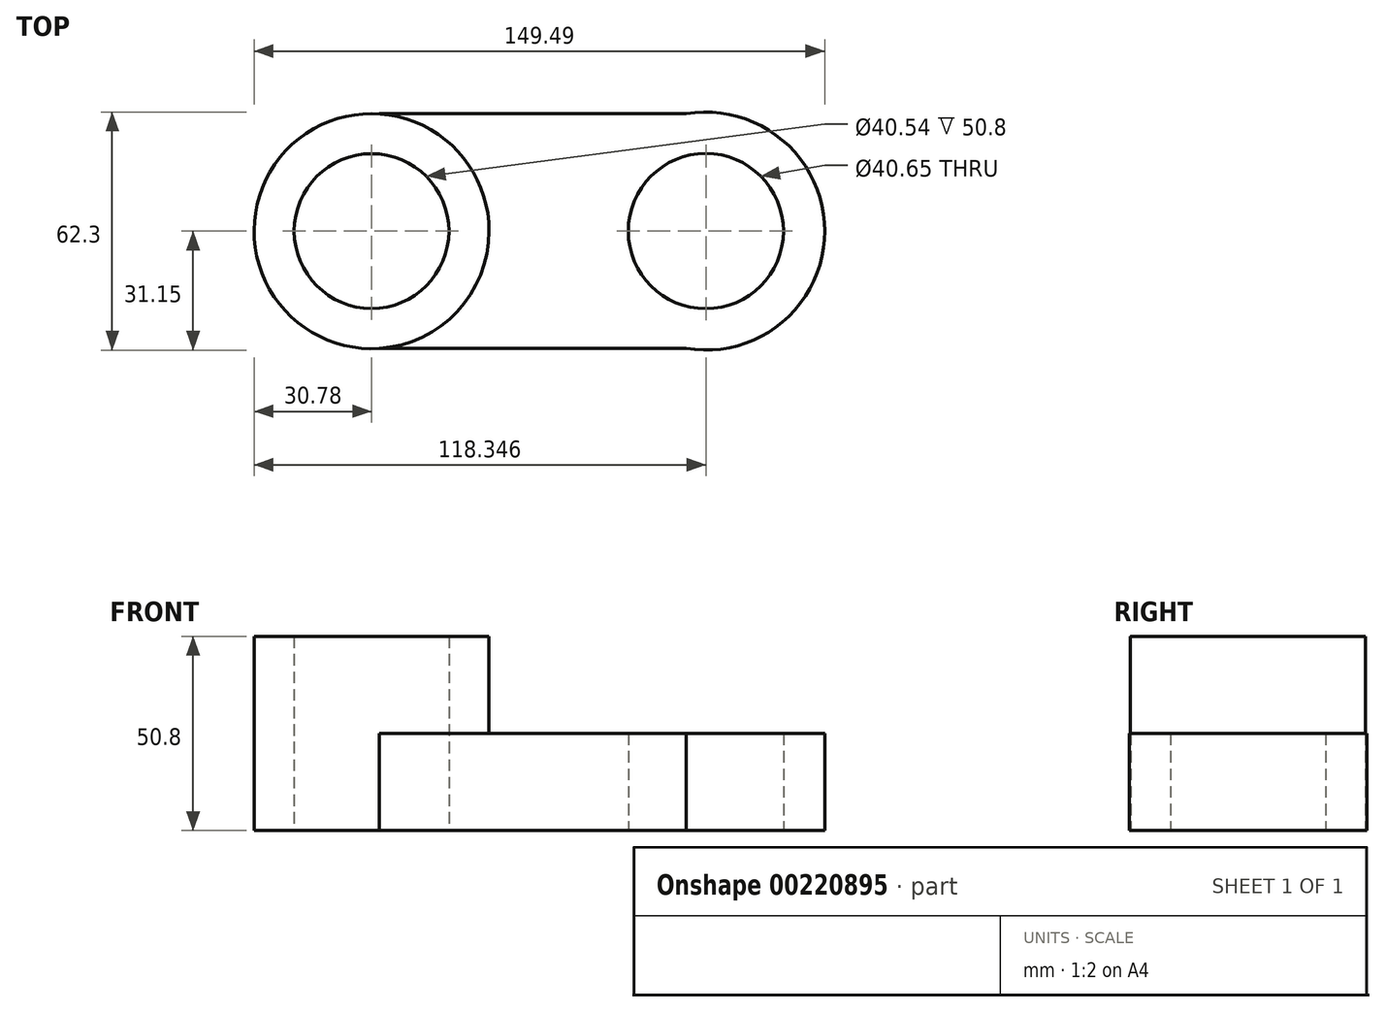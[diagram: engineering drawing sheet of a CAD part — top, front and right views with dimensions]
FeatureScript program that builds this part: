
annotation { "Feature Type Name" : "Feature", "Feature Type Description" : "" }
export const myFeature = defineFeature(function(context is Context, id is Id, definition is map)
    precondition{}
    {
        {
            var Q0;
            Q0=qCreatedBy(makeId("Top.planeOp"),FACE);
            var sketch = newSketch(context, id + "F0", { "sketchPlane" : qUnion([Q0])});
            skCircle(sketch, "E0", {"center": v(-44.77, 0) * mm, "radius": 30.78 * mm});
            skCircle(sketch, "E1", {"center": v(-44.77, 0) * mm, "radius": 20.27 * mm});
            skLineSegment(sketch, "E2.bottom", {"start": v(-42.8, 30.71) * mm, "end": v(42.8, 30.71) * mm});
            skLineSegment(sketch, "E2.top", {"start": v(-42.8, -30.71) * mm, "end": v(42.8, -30.71) * mm});
            skPoint(sketch, "E2.middle", {"position": v(0, 0) * mm});
            skArc(sketch, "E3", {"start": v(37.63, -30.71) * mm, "mid": v(73.94, 0) * mm, "end": v(37.63, 30.71) * mm});
            skCircle(sketch, "E4", {"center": v(42.8, 0) * mm, "radius": 20.33 * mm});
            skSolve(sketch);
        }
        {
            var Q0;
            Q0=makeQuery(id+"F0.imprint","IMPRINT",FACE,{"disambiguationData":[TD([[makeQuery(id+"F0.imprint","IMPRINT",EDGE,{"derivedFrom":sQuery(id+"F0.wireOp",EDGE,"E1")}),-1.0]])]});
            extrude(context, id + "F1", {"entities" : qUnion([Q0]), "depth" : 50.8 * mm});
        }
        {
            var Q0;
            {var subQ0=sQuery(id+"F0.wireOp",EDGE,"E3");Q0=makeQuery(id+"F0.imprint","IMPRINT",FACE,{"disambiguationData":[TD([[makeQuery(id+"F0.imprint","IMPRINT",EDGE,{"derivedFrom":subQ0}),1.0]])]});}
            extrude(context, id + "F2", {"entities" : qUnion([Q0]), "operationType" : NewBodyOperationType.ADD, "depth" : 25.4 * mm});
        }
    });
